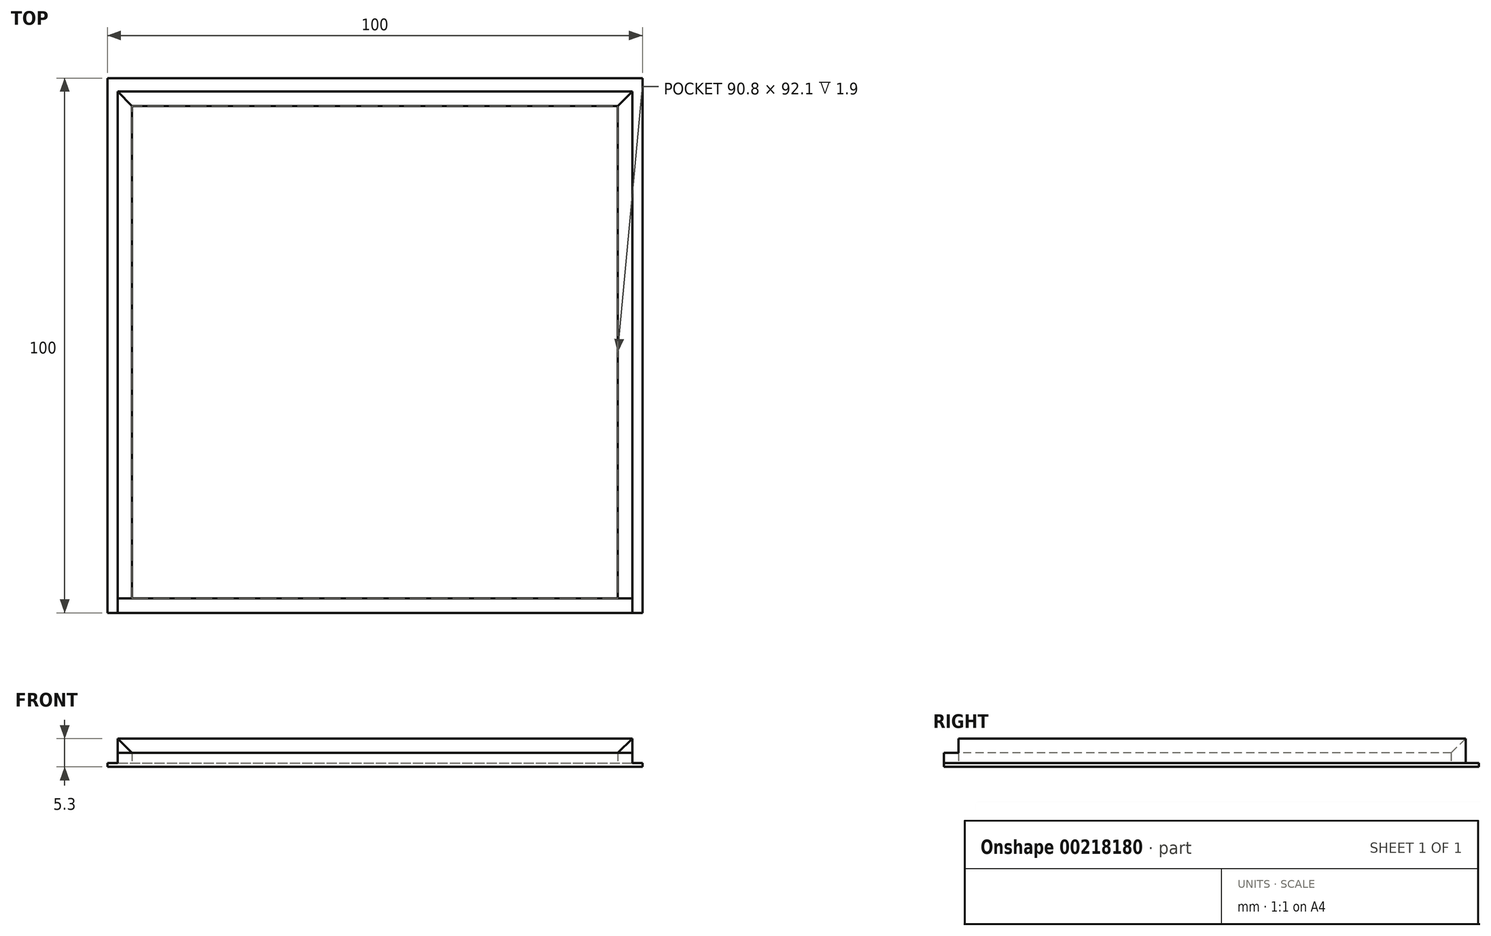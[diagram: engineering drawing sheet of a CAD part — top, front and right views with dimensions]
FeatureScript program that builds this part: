
annotation { "Feature Type Name" : "Feature", "Feature Type Description" : "" }
export const myFeature = defineFeature(function(context is Context, id is Id, definition is map)
    precondition{}
    {
        {
            var Q0;
            Q0=qCreatedBy(makeId("Top.planeOp"),FACE);
            var sketch = newSketch(context, id + "F0", { "sketchPlane" : qUnion([Q0])});
            skLineSegment(sketch, "E0.bottom", {"start": v(-50, 50) * mm, "end": v(50, 50) * mm});
            skLineSegment(sketch, "E0.top", {"start": v(-50, -50) * mm, "end": v(50, -50) * mm});
            skLineSegment(sketch, "E0.left", {"start": v(-50, 50) * mm, "end": v(-50, -50) * mm});
            skLineSegment(sketch, "E0.right", {"start": v(50, 50) * mm, "end": v(50, -50) * mm});
            skPoint(sketch, "E0.middle", {"position": v(0, 0) * mm});
            skSolve(sketch);
        }
        {
            var Q0;
            Q0 = qSketchRegion(id + "F0", true);
            extrude(context, id + "F1", {"entities" : qUnion([Q0]), "depth" : 0.7 * mm});
        }
        {
            var Q0;
            Q0=makeQuery(id+"F1.opExtrude","CAP_FACE",FACE,{"disambiguationData":[OSD([sQuery(id+"F0.wireOp",EDGE,"E0.bottom"),sQuery(id+"F0.wireOp",EDGE,"E0.top"),sQuery(id+"F0.wireOp",EDGE,"E0.left"),sQuery(id+"F0.wireOp",EDGE,"E0.right")])],"isStart":false});
            var sketch = newSketch(context, id + "F2", { "sketchPlane" : qUnion([Q0])});
            skLineSegment(sketch, "E1.bottom", {"start": v(-48.1, -50) * mm, "end": v(48.1, -50) * mm});
            skLineSegment(sketch, "E1.top", {"start": v(-48.1, 47.5) * mm, "end": v(48.1, 47.5) * mm});
            skLineSegment(sketch, "E1.left", {"start": v(-48.1, -50) * mm, "end": v(-48.1, 47.5) * mm});
            skLineSegment(sketch, "E1.right", {"start": v(48.1, -50) * mm, "end": v(48.1, 47.5) * mm});
            skLineSegment(sketch, "E2", {"start": v(-48.1, -1.25) * mm, "end": v(48.1, -1.25) * mm, "construction": true});
            skLineSegment(sketch, "E3", {"start": v(0, 47.5) * mm, "end": v(0, -50) * mm, "construction": true});
            skLineSegment(sketch, "E4.0", {"start": v(-45.4, 44.8) * mm, "end": v(45.4, 44.8) * mm});
            skLineSegment(sketch, "E4.1", {"start": v(-45.4, -47.3) * mm, "end": v(-45.4, 44.8) * mm});
            skLineSegment(sketch, "E4.2", {"start": v(-45.4, -47.3) * mm, "end": v(45.4, -47.3) * mm});
            skLineSegment(sketch, "E4.3", {"start": v(45.4, -47.3) * mm, "end": v(45.4, 44.8) * mm});
            skSolve(sketch);
        }
        {
            var Q0;
            Q0 = qSketchRegion(id + "F2", true);
            extrude(context, id + "F3", {"entities" : qUnion([Q0]), "operationType" : NewBodyOperationType.ADD, "depth" : 1.9 * mm});
        }
        {
            var Q0;
            Q0=makeQuery(id+"F3.opExtrude","CAP_FACE",FACE,{"disambiguationData":[OSD([sQuery(id+"F2.wireOp",EDGE,"E1.bottom"),sQuery(id+"F2.wireOp",EDGE,"E1.top"),sQuery(id+"F2.wireOp",EDGE,"E1.left"),sQuery(id+"F2.wireOp",EDGE,"E1.right"),sQuery(id+"F2.wireOp",EDGE,"E4.0"),sQuery(id+"F2.wireOp",EDGE,"E4.1"),sQuery(id+"F2.wireOp",EDGE,"E4.2"),sQuery(id+"F2.wireOp",EDGE,"E4.3")])],"isStart":false});
            var sketch = newSketch(context, id + "F4", { "sketchPlane" : qUnion([Q0])});
            skLineSegment(sketch, "E5", {"start": v(-45.4, -47.3) * mm, "end": v(-48.1, -47.3) * mm});
            skLineSegment(sketch, "E6", {"start": v(-48.1, -47.3) * mm, "end": v(-48.1, 47.5) * mm});
            skLineSegment(sketch, "E7", {"start": v(-48.1, 47.5) * mm, "end": v(48.1, 47.5) * mm});
            skLineSegment(sketch, "E8", {"start": v(48.1, 47.5) * mm, "end": v(48.1, -47.3) * mm});
            skLineSegment(sketch, "E9", {"start": v(48.1, -47.3) * mm, "end": v(45.4, -47.3) * mm});
            skLineSegment(sketch, "E10", {"start": v(45.4, -47.3) * mm, "end": v(45.4, 44.8) * mm});
            skLineSegment(sketch, "E11", {"start": v(45.4, 44.8) * mm, "end": v(-45.4, 44.8) * mm});
            skLineSegment(sketch, "E12", {"start": v(-45.4, 44.8) * mm, "end": v(-45.4, -47.3) * mm});
            skSolve(sketch);
        }
        {
            var Q0;
            Q0 = qSketchRegion(id + "F4", true);
            extrude(context, id + "F5", {"entities" : qUnion([Q0]), "operationType" : NewBodyOperationType.ADD, "depth" : 3 * mm});
        }
        {
            var Q0;
            Q0=makeQuery(id+"F5.opExtrude","CAP_EDGE",EDGE,{"disambiguationData":[OSD([sQuery(id+"F4.wireOp",EDGE,"E11")])],"isStart":false});
            var Q1;
            Q1=makeQuery(id+"F5.opExtrude","CAP_EDGE",EDGE,{"disambiguationData":[OSD([sQuery(id+"F4.wireOp",EDGE,"E12")])],"isStart":false});
            var Q2;
            Q2=makeQuery(id+"F5.opExtrude","CAP_EDGE",EDGE,{"disambiguationData":[OSD([sQuery(id+"F4.wireOp",EDGE,"E10")])],"isStart":false});
            chamfer(context, id + "F6", {"entities" : qUnion([Q0, Q1, Q2]), "width" : 3 * mm, "tangentPropagation" : true});
        }
    });
